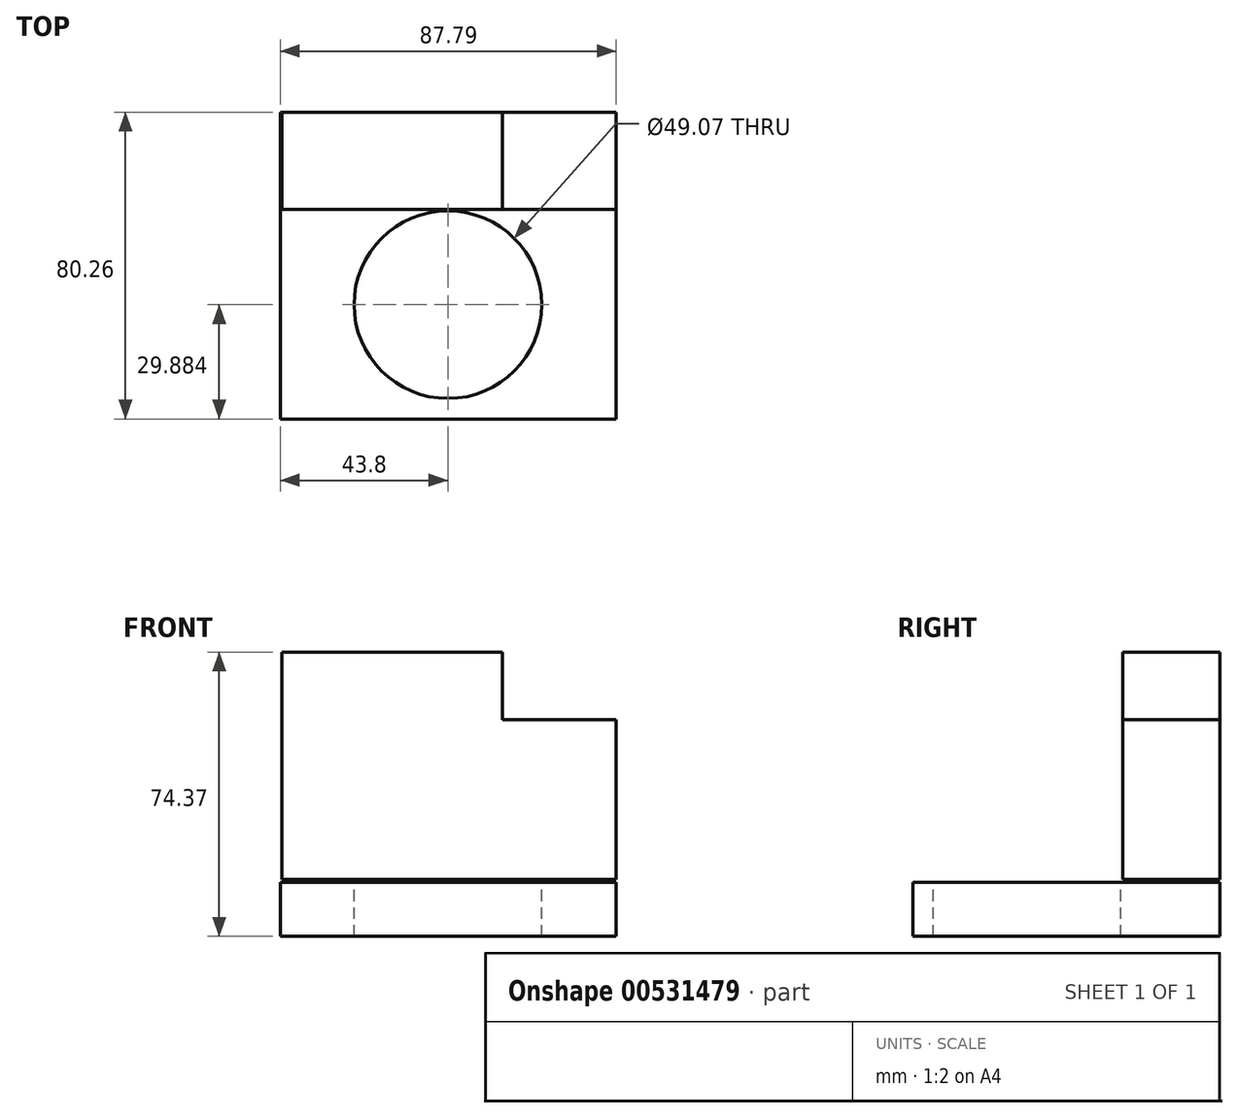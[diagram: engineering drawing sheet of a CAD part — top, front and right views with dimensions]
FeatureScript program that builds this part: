
annotation { "Feature Type Name" : "Feature", "Feature Type Description" : "" }
export const myFeature = defineFeature(function(context is Context, id is Id, definition is map)
    precondition{}
    {
        {
            var Q0;
            Q0=qCreatedBy(makeId("Front.planeOp"),FACE);
            var sketch = newSketch(context, id + "F0", { "sketchPlane" : qUnion([Q0])});
            skLineSegment(sketch, "E0.bottom", {"start": v(0, 0) * mm, "end": v(-87.33, 0) * mm});
            skLineSegment(sketch, "E0.top", {"start": v(0, -59.5) * mm, "end": v(-87.33, -59.5) * mm});
            skLineSegment(sketch, "E0.left", {"start": v(0, 0) * mm, "end": v(0, -59.5) * mm});
            skLineSegment(sketch, "E0.right", {"start": v(-87.33, 0) * mm, "end": v(-87.33, -59.5) * mm});
            skSolve(sketch);
        }
        {
            var Q0;
            Q0 = qSketchRegion(id + "F0", true);
            extrude(context, id + "F1", {"entities" : qUnion([Q0]), "depth" : 25.4 * mm, "offsetDistance" : 25.4 * mm});
        }
        {
            var Q0;
            Q0=qCreatedBy(makeId("Front.planeOp"),FACE);
            var sketch = newSketch(context, id + "F2", { "sketchPlane" : qUnion([Q0])});
            skLineSegment(sketch, "E1.bottom", {"start": v(0, 0) * mm, "end": v(-29.73, 0) * mm});
            skLineSegment(sketch, "E1.top", {"start": v(0, -17.68) * mm, "end": v(-29.73, -17.68) * mm});
            skLineSegment(sketch, "E1.left", {"start": v(0, 0) * mm, "end": v(0, -17.68) * mm});
            skLineSegment(sketch, "E1.right", {"start": v(-29.73, 0) * mm, "end": v(-29.73, -17.68) * mm});
            skSolve(sketch);
        }
        {
            var Q0;
            Q0 = qSketchRegion(id + "F2", true);
            extrude(context, id + "F3", {"entities" : qUnion([Q0]), "operationType" : NewBodyOperationType.REMOVE, "endBound" : BoundingType.THROUGH_ALL, "depth" : 25.4 * mm, "offsetDistance" : 25.4 * mm});
        }
        {
            var Q0;
            Q0=qCreatedBy(makeId("Front.planeOp"),FACE);
            var sketch = newSketch(context, id + "F4", { "sketchPlane" : qUnion([Q0])});
            skLineSegment(sketch, "E2.bottom", {"start": v(0, -60.17) * mm, "end": v(-87.79, -60.17) * mm});
            skLineSegment(sketch, "E2.top", {"start": v(0, -74.37) * mm, "end": v(-87.79, -74.37) * mm});
            skLineSegment(sketch, "E2.left", {"start": v(0, -60.17) * mm, "end": v(0, -74.37) * mm});
            skLineSegment(sketch, "E2.right", {"start": v(-87.79, -60.17) * mm, "end": v(-87.79, -74.37) * mm});
            skSolve(sketch);
        }
        {
            var Q0;
            Q0 = qSketchRegion(id + "F4", true);
            extrude(context, id + "F5", {"entities" : qUnion([Q0]), "depth" : 25.4 * mm, "offsetDistance" : 25.4 * mm});
        }
        {
            var Q0;
            Q0=makeQuery(id+"F5.opExtrude","CAP_FACE",FACE,{"disambiguationData":[OSD([sQuery(id+"F4.wireOp",EDGE,"E2.bottom"),sQuery(id+"F4.wireOp",EDGE,"E2.top"),sQuery(id+"F4.wireOp",EDGE,"E2.left"),sQuery(id+"F4.wireOp",EDGE,"E2.right")])],"isStart":false});
            extrude(context, id + "F6", {"entities" : qUnion([Q0]), "operationType" : NewBodyOperationType.ADD, "depth" : 54.86 * mm, "offsetDistance" : 25.4 * mm});
        }
        {
            var Q0;
            Q0=qCreatedBy(makeId("Top.planeOp"),FACE);
            var sketch = newSketch(context, id + "F7", { "sketchPlane" : qUnion([Q0])});
            skCircle(sketch, "E3", {"center": v(-44, -50.38) * mm, "radius": 24.54 * mm});
            skSolve(sketch);
        }
        {
            var Q0;
            Q0=makeQuery(id+"F7.imprint","IMPRINT",FACE,{"disambiguationData":[TD([[makeQuery(id+"F7.imprint","IMPRINT",EDGE,{"derivedFrom":sQuery(id+"F7.wireOp",EDGE,"E3")}),1.0]])]});
            extrude(context, id + "F8", {"entities" : qUnion([Q0]), "operationType" : NewBodyOperationType.REMOVE, "endBound" : BoundingType.THROUGH_ALL, "oppositeDirection" : true, "depth" : 25.4 * mm, "offsetDistance" : 25.4 * mm});
        }
    });
